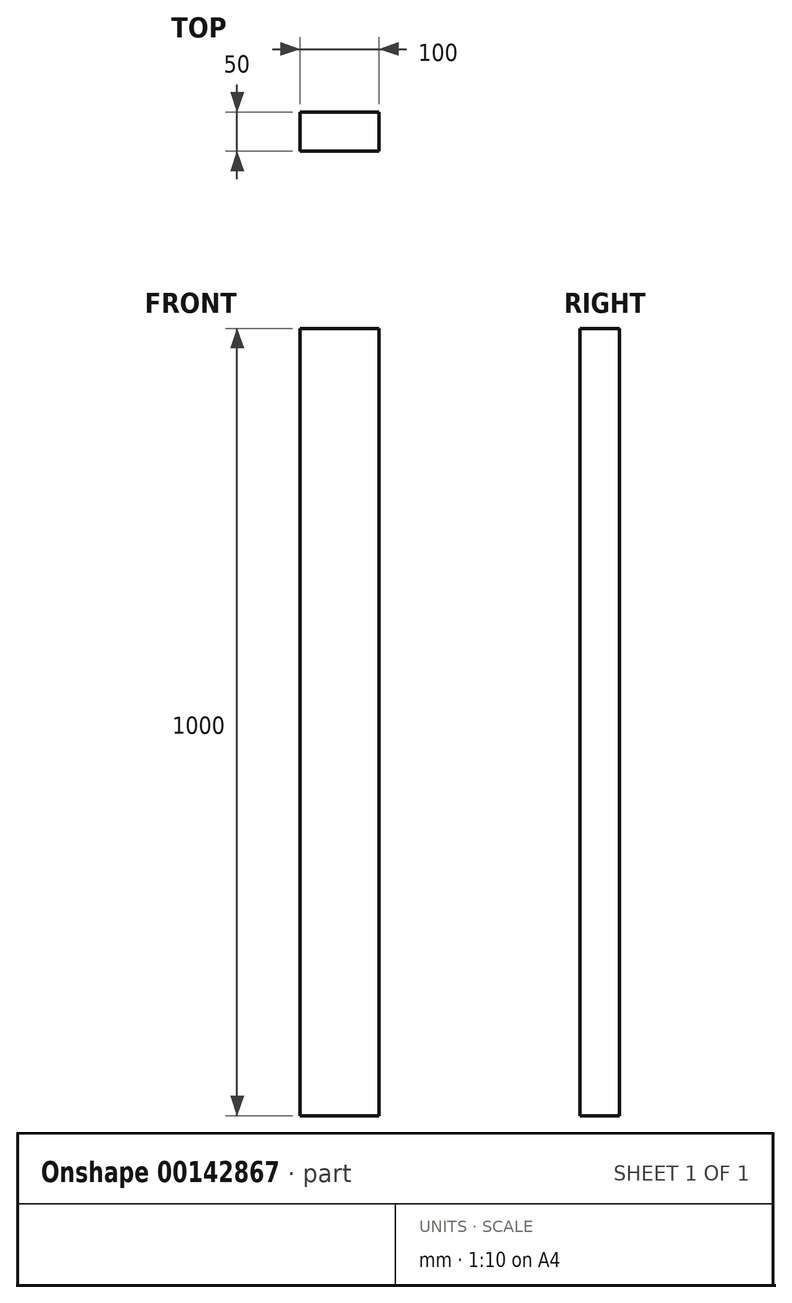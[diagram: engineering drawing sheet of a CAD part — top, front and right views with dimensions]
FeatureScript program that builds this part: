
annotation { "Feature Type Name" : "Feature", "Feature Type Description" : "" }
export const myFeature = defineFeature(function(context is Context, id is Id, definition is map)
    precondition{}
    {
        {
            var Q0;
            Q0=qCreatedBy(makeId("Top.planeOp"),FACE);
            var sketch = newSketch(context, id + "F0", { "sketchPlane" : qUnion([Q0])});
            skLineSegment(sketch, "E0.bottom", {"start": v(50, -25) * mm, "end": v(-50, -25) * mm});
            skLineSegment(sketch, "E0.top", {"start": v(50, 25) * mm, "end": v(-50, 25) * mm});
            skLineSegment(sketch, "E0.left", {"start": v(50, -25) * mm, "end": v(50, 25) * mm});
            skLineSegment(sketch, "E0.right", {"start": v(-50, -25) * mm, "end": v(-50, 25) * mm});
            skPoint(sketch, "E0.middle", {"position": v(0, 0) * mm});
            skSolve(sketch);
        }
        {
            var Q0;
            Q0=qSketchRegion(id+"F0",true);
            extrude(context, id + "F1", {"entities" : qUnion([Q0]), "depth" : 1000 * mm});
        }
    });
